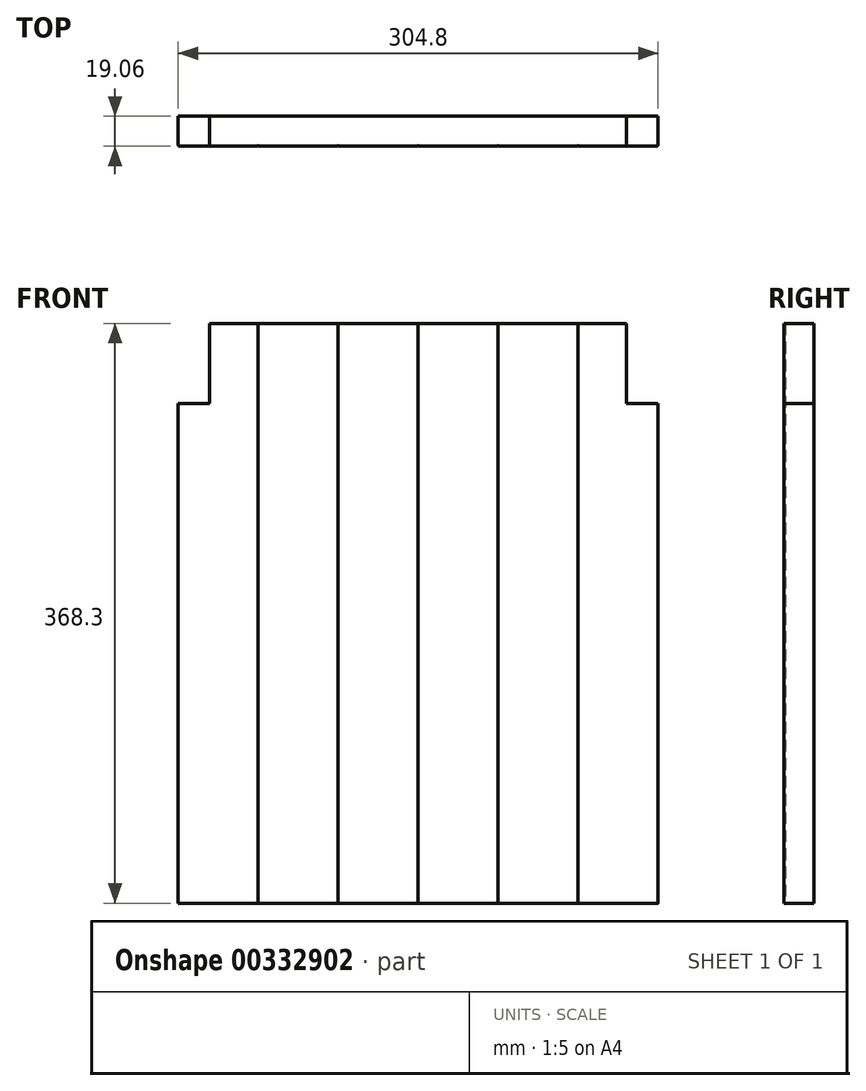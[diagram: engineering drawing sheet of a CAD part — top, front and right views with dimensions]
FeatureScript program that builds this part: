
annotation { "Feature Type Name" : "Feature", "Feature Type Description" : "" }
export const myFeature = defineFeature(function(context is Context, id is Id, definition is map)
    precondition{}
    {
        {
            var Q0;
            Q0=qCreatedBy(makeId("Top.planeOp"),FACE);
            var sketch = newSketch(context, id + "F0", { "sketchPlane" : qUnion([Q0])});
            skLineSegment(sketch, "E0.bottom", {"start": v(533.4, -9.53) * mm, "end": v(458.22, -9.53) * mm});
            skLineSegment(sketch, "E0.top", {"start": v(533.4, 9.53) * mm, "end": v(-533.4, 9.53) * mm});
            skLineSegment(sketch, "E0.left", {"start": v(533.4, 9.53) * mm, "end": v(533.4, -9.53) * mm});
            skLineSegment(sketch, "E0.right", {"start": v(-533.4, 9.53) * mm, "end": v(-533.4, -9.53) * mm});
            skPoint(sketch, "E0.middle", {"position": v(0, 0) * mm});
            skArc(sketch, "E1", {"start": v(-509.02, -9.53) * mm, "mid": v(-508.3, -9.23) * mm, "end": v(-508, -8.5) * mm});
            skArc(sketch, "E2", {"start": v(-508, -8.5) * mm, "mid": v(-507.7, -9.23) * mm, "end": v(-506.98, -9.52) * mm});
            skArc(sketch, "E3.1.0.0", {"start": v(-458.22, -9.53) * mm, "mid": v(-457.5, -9.23) * mm, "end": v(-457.2, -8.5) * mm});
            skArc(sketch, "E3.1.0.1", {"start": v(-457.2, -8.5) * mm, "mid": v(-456.9, -9.23) * mm, "end": v(-456.18, -9.52) * mm});
            skArc(sketch, "E3.2.0.0", {"start": v(-407.42, -9.53) * mm, "mid": v(-406.7, -9.23) * mm, "end": v(-406.4, -8.5) * mm});
            skArc(sketch, "E3.2.0.1", {"start": v(-406.4, -8.5) * mm, "mid": v(-406.1, -9.23) * mm, "end": v(-405.38, -9.52) * mm});
            skArc(sketch, "E3.3.0.0", {"start": v(-356.62, -9.53) * mm, "mid": v(-355.9, -9.23) * mm, "end": v(-355.6, -8.5) * mm});
            skArc(sketch, "E3.3.0.1", {"start": v(-355.6, -8.5) * mm, "mid": v(-355.3, -9.23) * mm, "end": v(-354.58, -9.52) * mm});
            skArc(sketch, "E3.4.0.0", {"start": v(-305.82, -9.53) * mm, "mid": v(-305.1, -9.23) * mm, "end": v(-304.8, -8.5) * mm});
            skArc(sketch, "E3.4.0.1", {"start": v(-304.8, -8.5) * mm, "mid": v(-304.5, -9.23) * mm, "end": v(-303.78, -9.52) * mm});
            skArc(sketch, "E3.5.0.0", {"start": v(-255.02, -9.53) * mm, "mid": v(-254.3, -9.23) * mm, "end": v(-254, -8.5) * mm});
            skArc(sketch, "E3.5.0.1", {"start": v(-254, -8.5) * mm, "mid": v(-253.7, -9.23) * mm, "end": v(-252.98, -9.52) * mm});
            skArc(sketch, "E3.6.0.0", {"start": v(-204.22, -9.53) * mm, "mid": v(-203.5, -9.23) * mm, "end": v(-203.2, -8.5) * mm});
            skArc(sketch, "E3.6.0.1", {"start": v(-203.2, -8.5) * mm, "mid": v(-202.9, -9.23) * mm, "end": v(-202.18, -9.52) * mm});
            skArc(sketch, "E3.7.0.0", {"start": v(-153.42, -9.53) * mm, "mid": v(-152.7, -9.23) * mm, "end": v(-152.4, -8.5) * mm});
            skArc(sketch, "E3.7.0.1", {"start": v(-152.4, -8.5) * mm, "mid": v(-152.1, -9.23) * mm, "end": v(-151.38, -9.52) * mm});
            skArc(sketch, "E3.8.0.0", {"start": v(-102.62, -9.53) * mm, "mid": v(-101.9, -9.23) * mm, "end": v(-101.6, -8.5) * mm});
            skArc(sketch, "E3.8.0.1", {"start": v(-101.6, -8.5) * mm, "mid": v(-101.3, -9.23) * mm, "end": v(-100.58, -9.52) * mm});
            skArc(sketch, "E3.9.0.0", {"start": v(-51.82, -9.53) * mm, "mid": v(-51.1, -9.23) * mm, "end": v(-50.8, -8.5) * mm});
            skArc(sketch, "E3.9.0.1", {"start": v(-50.8, -8.5) * mm, "mid": v(-50.5, -9.23) * mm, "end": v(-49.78, -9.52) * mm});
            skArc(sketch, "E3.10.0.0", {"start": v(-1.02, -9.53) * mm, "mid": v(-0.3, -9.23) * mm, "end": v(0, -8.5) * mm});
            skArc(sketch, "E3.10.0.1", {"start": v(0, -8.5) * mm, "mid": v(0.3, -9.23) * mm, "end": v(1.02, -9.52) * mm});
            skArc(sketch, "E3.11.0.0", {"start": v(49.78, -9.53) * mm, "mid": v(50.5, -9.23) * mm, "end": v(50.8, -8.5) * mm});
            skArc(sketch, "E3.11.0.1", {"start": v(50.8, -8.5) * mm, "mid": v(51.1, -9.23) * mm, "end": v(51.82, -9.52) * mm});
            skArc(sketch, "E3.12.0.0", {"start": v(100.58, -9.53) * mm, "mid": v(101.3, -9.23) * mm, "end": v(101.6, -8.5) * mm});
            skArc(sketch, "E3.12.0.1", {"start": v(101.6, -8.5) * mm, "mid": v(101.9, -9.23) * mm, "end": v(102.62, -9.52) * mm});
            skArc(sketch, "E3.13.0.0", {"start": v(151.38, -9.53) * mm, "mid": v(152.1, -9.23) * mm, "end": v(152.4, -8.5) * mm});
            skArc(sketch, "E3.13.0.1", {"start": v(152.4, -8.5) * mm, "mid": v(152.7, -9.23) * mm, "end": v(153.42, -9.52) * mm});
            skArc(sketch, "E3.14.0.0", {"start": v(202.18, -9.53) * mm, "mid": v(202.9, -9.23) * mm, "end": v(203.2, -8.5) * mm});
            skArc(sketch, "E3.14.0.1", {"start": v(203.2, -8.5) * mm, "mid": v(203.5, -9.23) * mm, "end": v(204.22, -9.52) * mm});
            skArc(sketch, "E3.15.0.0", {"start": v(252.98, -9.53) * mm, "mid": v(253.7, -9.23) * mm, "end": v(254, -8.5) * mm});
            skArc(sketch, "E3.15.0.1", {"start": v(254, -8.5) * mm, "mid": v(254.3, -9.23) * mm, "end": v(255.02, -9.52) * mm});
            skArc(sketch, "E3.16.0.0", {"start": v(303.78, -9.53) * mm, "mid": v(304.5, -9.23) * mm, "end": v(304.8, -8.5) * mm});
            skArc(sketch, "E3.16.0.1", {"start": v(304.8, -8.5) * mm, "mid": v(305.1, -9.23) * mm, "end": v(305.82, -9.52) * mm});
            skArc(sketch, "E3.17.0.0", {"start": v(354.58, -9.53) * mm, "mid": v(355.3, -9.23) * mm, "end": v(355.6, -8.5) * mm});
            skArc(sketch, "E3.17.0.1", {"start": v(355.6, -8.5) * mm, "mid": v(355.9, -9.23) * mm, "end": v(356.62, -9.52) * mm});
            skArc(sketch, "E3.18.0.0", {"start": v(405.38, -9.53) * mm, "mid": v(406.1, -9.23) * mm, "end": v(406.4, -8.5) * mm});
            skArc(sketch, "E3.18.0.1", {"start": v(406.4, -8.5) * mm, "mid": v(406.7, -9.23) * mm, "end": v(407.42, -9.52) * mm});
            skArc(sketch, "E3.19.0.0", {"start": v(456.18, -9.53) * mm, "mid": v(456.9, -9.23) * mm, "end": v(457.2, -8.5) * mm});
            skArc(sketch, "E3.19.0.1", {"start": v(457.2, -8.5) * mm, "mid": v(457.5, -9.23) * mm, "end": v(458.22, -9.52) * mm});
            skLineSegment(sketch, "E3.direction1", {"start": v(-506.98, -9.53) * mm, "end": v(-458.22, -9.53) * mm, "construction": true});
            skLineSegment(sketch, "E4.trimOffspring", {"start": v(-458.22, -9.53) * mm, "end": v(-533.4, -9.53) * mm});
            skLineSegment(sketch, "E5.trimOffspring", {"start": v(-407.42, -9.53) * mm, "end": v(-456.18, -9.53) * mm});
            skLineSegment(sketch, "E6.trimOffspring", {"start": v(-356.62, -9.53) * mm, "end": v(-405.38, -9.53) * mm});
            skLineSegment(sketch, "E7.trimOffspring", {"start": v(-305.82, -9.53) * mm, "end": v(-354.58, -9.53) * mm});
            skLineSegment(sketch, "E8.trimOffspring", {"start": v(-255.02, -9.53) * mm, "end": v(-303.78, -9.53) * mm});
            skLineSegment(sketch, "E9.trimOffspring", {"start": v(-204.22, -9.53) * mm, "end": v(-252.98, -9.53) * mm});
            skLineSegment(sketch, "E10.trimOffspring", {"start": v(-153.42, -9.53) * mm, "end": v(-202.18, -9.53) * mm});
            skLineSegment(sketch, "E11.trimOffspring", {"start": v(-102.62, -9.53) * mm, "end": v(-151.38, -9.53) * mm});
            skLineSegment(sketch, "E12.trimOffspring", {"start": v(-51.82, -9.53) * mm, "end": v(-100.58, -9.53) * mm});
            skLineSegment(sketch, "E13.trimOffspring", {"start": v(-1.02, -9.53) * mm, "end": v(-49.78, -9.53) * mm});
            skLineSegment(sketch, "E14.trimOffspring", {"start": v(49.78, -9.53) * mm, "end": v(1.02, -9.53) * mm});
            skLineSegment(sketch, "E15.trimOffspring", {"start": v(100.58, -9.53) * mm, "end": v(51.82, -9.53) * mm});
            skLineSegment(sketch, "E16.trimOffspring", {"start": v(151.38, -9.53) * mm, "end": v(102.62, -9.53) * mm});
            skLineSegment(sketch, "E17.trimOffspring", {"start": v(202.18, -9.53) * mm, "end": v(153.42, -9.53) * mm});
            skLineSegment(sketch, "E18.trimOffspring", {"start": v(252.98, -9.53) * mm, "end": v(204.22, -9.53) * mm});
            skLineSegment(sketch, "E19.trimOffspring", {"start": v(303.78, -9.53) * mm, "end": v(255.02, -9.53) * mm});
            skLineSegment(sketch, "E20.trimOffspring", {"start": v(354.58, -9.53) * mm, "end": v(305.82, -9.53) * mm});
            skLineSegment(sketch, "E21.trimOffspring", {"start": v(405.38, -9.53) * mm, "end": v(356.62, -9.53) * mm});
            skLineSegment(sketch, "E22.trimOffspring", {"start": v(456.18, -9.53) * mm, "end": v(407.42, -9.53) * mm});
            skSolve(sketch);
        }
        {
            var Q0;
            Q0=qSketchRegion(id+"F0",true);
            extrude(context, id + "F1", {"entities" : qUnion([Q0]), "depth" : 368.3 * mm});
        }
        {
            var Q0;
            Q0=qCreatedBy(makeId("Top.planeOp"),FACE);
            var sketch = newSketch(context, id + "F2", { "sketchPlane" : qUnion([Q0])});
            skLineSegment(sketch, "E23.bottom", {"start": v(-604.49, 134.84) * mm, "end": v(-152.4, 134.84) * mm});
            skLineSegment(sketch, "E23.top", {"start": v(-604.49, -165.86) * mm, "end": v(-152.4, -165.86) * mm});
            skLineSegment(sketch, "E23.left", {"start": v(-604.49, 134.84) * mm, "end": v(-604.49, -165.86) * mm});
            skLineSegment(sketch, "E23.right", {"start": v(-152.4, 134.84) * mm, "end": v(-152.4, -165.86) * mm});
            skLineSegment(sketch, "E24.bottom", {"start": v(602.44, 136.89) * mm, "end": v(152.4, 136.89) * mm});
            skLineSegment(sketch, "E24.top", {"start": v(602.44, -135.18) * mm, "end": v(152.4, -135.18) * mm});
            skLineSegment(sketch, "E24.left", {"start": v(602.44, 136.89) * mm, "end": v(602.44, -135.18) * mm});
            skLineSegment(sketch, "E24.right", {"start": v(152.4, 136.89) * mm, "end": v(152.4, -135.18) * mm});
            skSolve(sketch);
        }
        {
            var Q0;
            Q0 = qSketchRegion(id + "F2", true);
            extrude(context, id + "F3", {"entities" : qUnion([Q0]), "operationType" : NewBodyOperationType.REMOVE, "depth" : 381 * mm});
        }
        {
            var Q0;
            Q0=qCreatedBy(makeId("Front.planeOp"),FACE);
            var sketch = newSketch(context, id + "F4", { "sketchPlane" : qUnion([Q0])});
            skLineSegment(sketch, "E25.bottom", {"start": v(-178.72, 429.05) * mm, "end": v(-132.33, 429.05) * mm});
            skLineSegment(sketch, "E25.top", {"start": v(-178.72, 317.5) * mm, "end": v(-132.33, 317.5) * mm});
            skLineSegment(sketch, "E25.left", {"start": v(-178.72, 429.05) * mm, "end": v(-178.72, 317.5) * mm});
            skLineSegment(sketch, "E25.right", {"start": v(-132.33, 429.05) * mm, "end": v(-132.33, 317.5) * mm});
            skLineSegment(sketch, "E26.bottom", {"start": v(199.06, 448.39) * mm, "end": v(132.33, 448.39) * mm});
            skLineSegment(sketch, "E26.top", {"start": v(199.06, 317.5) * mm, "end": v(132.33, 317.5) * mm});
            skLineSegment(sketch, "E26.left", {"start": v(199.06, 448.39) * mm, "end": v(199.06, 317.5) * mm});
            skLineSegment(sketch, "E26.right", {"start": v(132.33, 448.39) * mm, "end": v(132.33, 317.5) * mm});
            skSolve(sketch);
        }
        {
            var Q0;
            Q0 = qSketchRegion(id + "F4", true);
            extrude(context, id + "F5", {"entities" : qUnion([Q0]), "operationType" : NewBodyOperationType.REMOVE, "endBound" : BoundingType.SYMMETRIC, "oppositeDirection" : true, "depth" : 25.4 * mm});
        }
    });
